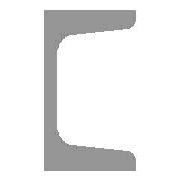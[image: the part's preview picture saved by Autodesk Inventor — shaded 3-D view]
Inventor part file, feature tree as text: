
AUTODESK INVENTOR PART (.ipt)
format: ipt  version: 2025 (Build 290162010, 162A)  size: 138,240 bytes
history: native  units: mm (DEFAULTED — no unit token found)
features: other x3, sketch x1, plane x1
ambient origin geometry x8: Origin, YZ Plane, XZ Plane, XY Plane, X Axis, Y Axis, Z Axis, Center Point
bodies: Solid1 (feature_tree), Body (feature_tree)
feature tree (5):
  other  "Driven Length"
  other  "Start plane"
  other  "End plane"
  sketch  "Sketch3"  dims[d0=5.5mm d1=40.0mm d2=45.0mm d3=7.5mm d4=19.75mm d5=2.075804mm d6=1300.0mm d7=0.0mm d23=8.0mm d24=4.0mm d25=1.43mm d26=-0.0mm d27=1300.0mm d28=90.0deg d29=1300.0mm]
  plane  "Work Plane3"
